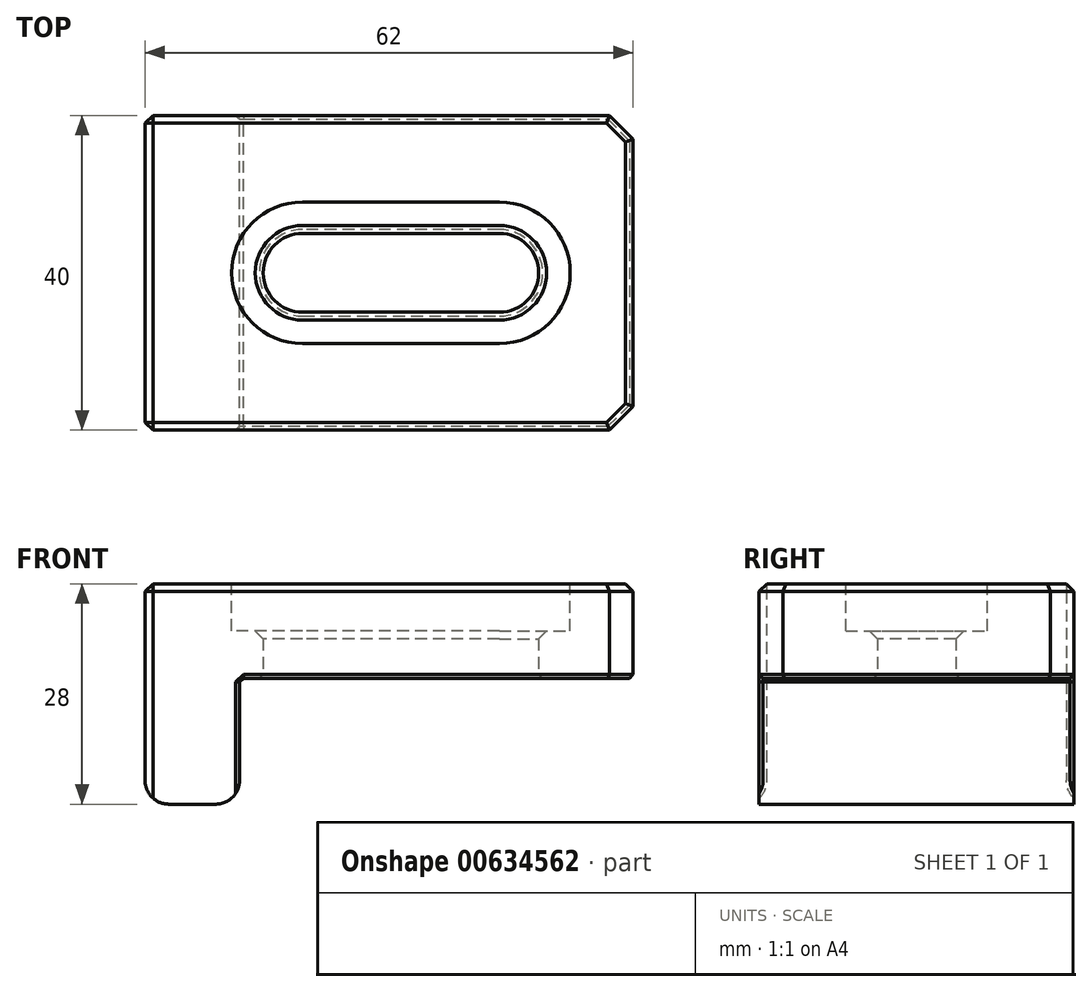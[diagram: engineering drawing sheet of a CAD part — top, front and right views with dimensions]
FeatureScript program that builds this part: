
annotation { "Feature Type Name" : "Feature", "Feature Type Description" : "" }
export const myFeature = defineFeature(function(context is Context, id is Id, definition is map)
    precondition{}
    {
        {
            var Q0;
            Q0=qCreatedBy(makeId("Front.planeOp"),FACE);
            var sketch = newSketch(context, id + "F0", { "sketchPlane" : qUnion([Q0])});
            skLineSegment(sketch, "E0", {"start": v(-35.7, 0) * mm, "end": v(-35.7, 28) * mm});
            skLineSegment(sketch, "E1", {"start": v(-35.7, 28) * mm, "end": v(26.3, 28) * mm});
            skLineSegment(sketch, "E2", {"start": v(26.3, 28) * mm, "end": v(26.3, 16) * mm});
            skLineSegment(sketch, "E3", {"start": v(26.3, 16) * mm, "end": v(-23.7, 16) * mm});
            skLineSegment(sketch, "E4", {"start": v(-23.7, 16) * mm, "end": v(-23.7, 0) * mm});
            skLineSegment(sketch, "E5", {"start": v(-23.7, 0) * mm, "end": v(-35.7, 0) * mm});
            skSolve(sketch);
        }
        {
            var Q0;
            Q0=makeQuery(id+"F0.imprint","IMPRINT",FACE,{"disambiguationData":[TD([[makeQuery(id+"F0.imprint","IMPRINT",EDGE,{"derivedFrom":sQuery(id+"F0.wireOp",EDGE,"E0")}),-1.0]])]});
            extrude(context, id + "F1", {"entities" : qUnion([Q0]), "endBound" : BoundingType.SYMMETRIC, "depth" : 40 * mm, "offsetDistance" : 25 * mm});
        }
        {
            var Q0;
            Q0=makeQuery(id+"F1.opExtrude","SWEPT_FACE",FACE,{"disambiguationData":[OSD([sQuery(id+"F0.wireOp",EDGE,"E1")])]});
            var sketch = newSketch(context, id + "F2", { "sketchPlane" : qUnion([Q0])});
            skLineSegment(sketch, "E6.bottom", {"start": v(-15.7, -5) * mm, "end": v(9.3, -5) * mm});
            skLineSegment(sketch, "E6.top", {"start": v(-15.7, 5) * mm, "end": v(9.3, 5) * mm});
            skLineSegment(sketch, "E6.left", {"start": v(-20.7, 0) * mm, "end": v(-20.7, 0) * mm});
            skLineSegment(sketch, "E6.right", {"start": v(14.3, 0) * mm, "end": v(14.3, 0) * mm});
            skPoint(sketch, "E6.middle", {"position": v(-3.2, 0) * mm});
            skPoint(sketch, "E7.visualSharp", {"position": v(-20.7, 5) * mm});
            skArc(sketch, "E7.filletArc", {"start": v(-15.7, 5) * mm, "mid": v(-19.24, 3.54) * mm, "end": v(-20.7, 0) * mm});
            skPoint(sketch, "E8.visualSharp", {"position": v(-20.7, -5) * mm});
            skArc(sketch, "E8.filletArc", {"start": v(-20.7, 0) * mm, "mid": v(-19.24, -3.54) * mm, "end": v(-15.7, -5) * mm});
            skPoint(sketch, "E9.visualSharp", {"position": v(14.3, 5) * mm});
            skArc(sketch, "E9.filletArc", {"start": v(14.3, 0) * mm, "mid": v(12.83, 3.54) * mm, "end": v(9.3, 5) * mm});
            skPoint(sketch, "E10.visualSharp", {"position": v(14.3, -5) * mm});
            skArc(sketch, "E10.filletArc", {"start": v(9.3, -5) * mm, "mid": v(12.83, -3.54) * mm, "end": v(14.3, 0) * mm});
            skLineSegment(sketch, "E11", {"start": v(-35.7, 0) * mm, "end": v(26.3, 0) * mm, "construction": true});
            skLineSegment(sketch, "E12", {"start": v(-8.94, 0) * mm, "end": v(-8.94, 5) * mm, "construction": true});
            skLineSegment(sketch, "E13", {"start": v(-8.94, 0) * mm, "end": v(-8.94, -5) * mm, "construction": true});
            skSolve(sketch);
        }
        {
            var Q0;
            Q0=makeQuery(id+"F2.imprint","IMPRINT",FACE,{"disambiguationData":[TD([[makeQuery(id+"F2.imprint","IMPRINT",EDGE,{"derivedFrom":sQuery(id+"F2.wireOp",EDGE,"E6.bottom")}),1.0]])]});
            extrude(context, id + "F3", {"entities" : qUnion([Q0]), "operationType" : NewBodyOperationType.REMOVE, "endBound" : BoundingType.SYMMETRIC, "depth" : 30 * mm, "offsetDistance" : 25 * mm});
        }
        {
            var Q0;
            Q0=makeQuery(id+"F1.opExtrude","CAP_EDGE",EDGE,{"disambiguationData":[OSD([sQuery(id+"F0.wireOp",EDGE,"E2")])],"isStart":false});
            var Q1;
            Q1=makeQuery(id+"F1.opExtrude","CAP_EDGE",EDGE,{"disambiguationData":[OSD([sQuery(id+"F0.wireOp",EDGE,"E2")])],"isStart":true});
            chamfer(context, id + "F4", {"entities" : qUnion([Q0, Q1]), "width" : 3 * mm, "tangentPropagation" : true});
        }
        {
            var Q0;
            Q0=makeQuery(id+"F1.opExtrude","CAP_EDGE",EDGE,{"disambiguationData":[OSD([sQuery(id+"F0.wireOp",EDGE,"E1")])],"isStart":false});
            var Q1;
            Q1=makeQuery(id+"F4.opChamfer","BLEND_EDGE",EDGE,{"blendedFrom":[makeQuery(id+"F1.opExtrude","CAP_EDGE",EDGE,{"disambiguationData":[OSD([sQuery(id+"F0.wireOp",EDGE,"E2")])],"isStart":false}),makeQuery(id+"F1.opExtrude","SWEPT_FACE",FACE,{"disambiguationData":[OSD([sQuery(id+"F0.wireOp",EDGE,"E1")])]})],"blendedInto":[makeQuery(id+"F1.opExtrude","SWEPT_FACE",FACE,{"disambiguationData":[OSD([sQuery(id+"F0.wireOp",EDGE,"E1")])]})]});
            var Q2;
            Q2=makeQuery(id+"F1.opExtrude","SWEPT_EDGE",EDGE,{"disambiguationData":[OSD([sQuery(id+"F0.wireOp",EDGE,"E1"),sQuery(id+"F0.wireOp",EDGE,"E2")])]});
            var Q3;
            Q3=makeQuery(id+"F1.opExtrude","SWEPT_FACE",FACE,{"disambiguationData":[OSD([sQuery(id+"F0.wireOp",EDGE,"E1")])]});
            var Q4;
            Q4=makeQuery(id+"F1.opExtrude","CAP_EDGE",EDGE,{"disambiguationData":[OSD([sQuery(id+"F0.wireOp",EDGE,"E0")])],"isStart":false});
            var Q5;
            Q5=makeQuery(id+"F1.opExtrude","CAP_EDGE",EDGE,{"disambiguationData":[OSD([sQuery(id+"F0.wireOp",EDGE,"E0")])],"isStart":true});
            chamfer(context, id + "F5", {"entities" : qUnion([Q0, Q1, Q2, Q3, Q4, Q5]), "width" : 1 * mm, "tangentPropagation" : true});
        }
        {
            var Q0;
            Q0=makeQuery(id+"F1.opExtrude","SWEPT_FACE",FACE,{"disambiguationData":[OSD([sQuery(id+"F0.wireOp",EDGE,"E3")])]});
            chamfer(context, id + "F6", {"entities" : qUnion([Q0]), "width" : 0.5 * mm, "tangentPropagation" : true});
        }
        {
            var Q0;
            Q0=makeQuery(id+"F1.opExtrude","SWEPT_FACE",FACE,{"disambiguationData":[OSD([sQuery(id+"F0.wireOp",EDGE,"E1")])]});
            var sketch = newSketch(context, id + "F7", { "sketchPlane" : qUnion([Q0])});
            skLineSegment(sketch, "E14.0", {"start": v(9.3, -9) * mm, "end": v(-15.7, -9) * mm});
            skArc(sketch, "E14.1", {"start": v(9.3, 9) * mm, "mid": v(18.3, 0) * mm, "end": v(9.3, -9) * mm});
            skLineSegment(sketch, "E14.2", {"start": v(-15.7, 9) * mm, "end": v(9.3, 9) * mm});
            skArc(sketch, "E14.3", {"start": v(-15.7, -9) * mm, "mid": v(-24.7, 0) * mm, "end": v(-15.7, 9) * mm});
            skSolve(sketch);
        }
        {
            var Q0;
            Q0=makeQuery(id+"F7.imprint","IMPRINT",FACE,{"disambiguationData":[TD([[makeQuery(id+"F7.imprint","IMPRINT",EDGE,{"derivedFrom":sQuery(id+"F7.wireOp",EDGE,"E14.0")}),-1.0]])]});
            var Q1;
            {var subQ0=makeQuery(id+"F1.opExtrude","SWEPT_FACE",FACE,{"disambiguationData":[OSD([sQuery(id+"F0.wireOp",EDGE,"E1")])]});var subQ1=subQ0;Q1=makeQuery(id+"F7.imprint","IMPRINT",FACE,{"disambiguationData":[TD([[makeQuery(id+"F7.imprint","IMPRINT",EDGE,{"derivedFrom":makeQuery(id+"F5.opChamfer","BLEND_EDGE",EDGE,{"blendedFrom":[makeQuery(id+"F3.boolean.opBoolean","INTERSECT",EDGE,{"derivedFrom":[subQ0,makeQuery(id+"F3.opExtrude","SWEPT_FACE",FACE,{"disambiguationData":[OSD([sQuery(id+"F2.wireOp",EDGE,"E6.bottom")])]})]}),subQ1],"blendedInto":[subQ1]})}),-1.0]])]});}
            extrude(context, id + "F8", {"entities" : qUnion([Q0, Q1]), "operationType" : NewBodyOperationType.REMOVE, "oppositeDirection" : true, "depth" : 6 * mm, "offsetDistance" : 25 * mm});
        }
        {
            var Q0;
            Q0=makeQuery(id+"F8.boolean.opBoolean","COPY",EDGE,{"derivedFrom":makeQuery(id+"F8.opExtrude","CAP_EDGE",EDGE,{"disambiguationData":[OSD([sQuery(id+"F7.wireOp",EDGE,"E14.3")])],"isStart":true})});
            var Q1;
            Q1=makeQuery(id+"F8.boolean.opBoolean","COPY",EDGE,{"derivedFrom":makeQuery(id+"F8.opExtrude","CAP_EDGE",EDGE,{"disambiguationData":[OSD([sQuery(id+"F7.wireOp",EDGE,"E14.2")])],"isStart":true})});
            var Q2;
            Q2=makeQuery(id+"F8.boolean.opBoolean","COPY",EDGE,{"derivedFrom":makeQuery(id+"F8.opExtrude","CAP_EDGE",EDGE,{"disambiguationData":[OSD([sQuery(id+"F7.wireOp",EDGE,"E14.0")])],"isStart":true})});
            var Q3;
            Q3=makeQuery(id+"F8.boolean.opBoolean","COPY",EDGE,{"derivedFrom":makeQuery(id+"F8.opExtrude","CAP_EDGE",EDGE,{"disambiguationData":[OSD([sQuery(id+"F7.wireOp",EDGE,"E14.1")])],"isStart":true})});
            var Q4;
            Q4=makeQuery(id+"F8.boolean.opBoolean","INTERSECT",EDGE,{"derivedFrom":[makeQuery(id+"F3.boolean.opBoolean","COPY",FACE,{"derivedFrom":makeQuery(id+"F3.opExtrude","SWEPT_FACE",FACE,{"disambiguationData":[OSD([sQuery(id+"F2.wireOp",EDGE,"E6.top")])]})}),makeQuery(id+"F8.opExtrude","CAP_FACE",FACE,{"disambiguationData":[OSD([sQuery(id+"F7.wireOp",EDGE,"E14.0"),sQuery(id+"F7.wireOp",EDGE,"E14.1"),sQuery(id+"F7.wireOp",EDGE,"E14.2"),sQuery(id+"F7.wireOp",EDGE,"E14.3")])],"isStart":false})]});
            chamfer(context, id + "F9", {"entities" : qUnion([Q0, Q1, Q2, Q3, Q4]), "width" : 1 * mm, "tangentPropagation" : true});
        }
        {
            var Q0;
            Q0=makeQuery(id+"F1.opExtrude","SWEPT_EDGE",EDGE,{"disambiguationData":[OSD([sQuery(id+"F0.wireOp",EDGE,"E4"),sQuery(id+"F0.wireOp",EDGE,"E5")])]});
            var Q1;
            Q1=makeQuery(id+"F1.opExtrude","SWEPT_EDGE",EDGE,{"disambiguationData":[OSD([sQuery(id+"F0.wireOp",EDGE,"E0"),sQuery(id+"F0.wireOp",EDGE,"E5")])]});
            fillet(context, id + "F10", {"entities" : qUnion([Q0, Q1]), "radius" : 3 * mm, "tangentPropagation" : true, "allowEdgeOverflow" : false});
        }
    });
